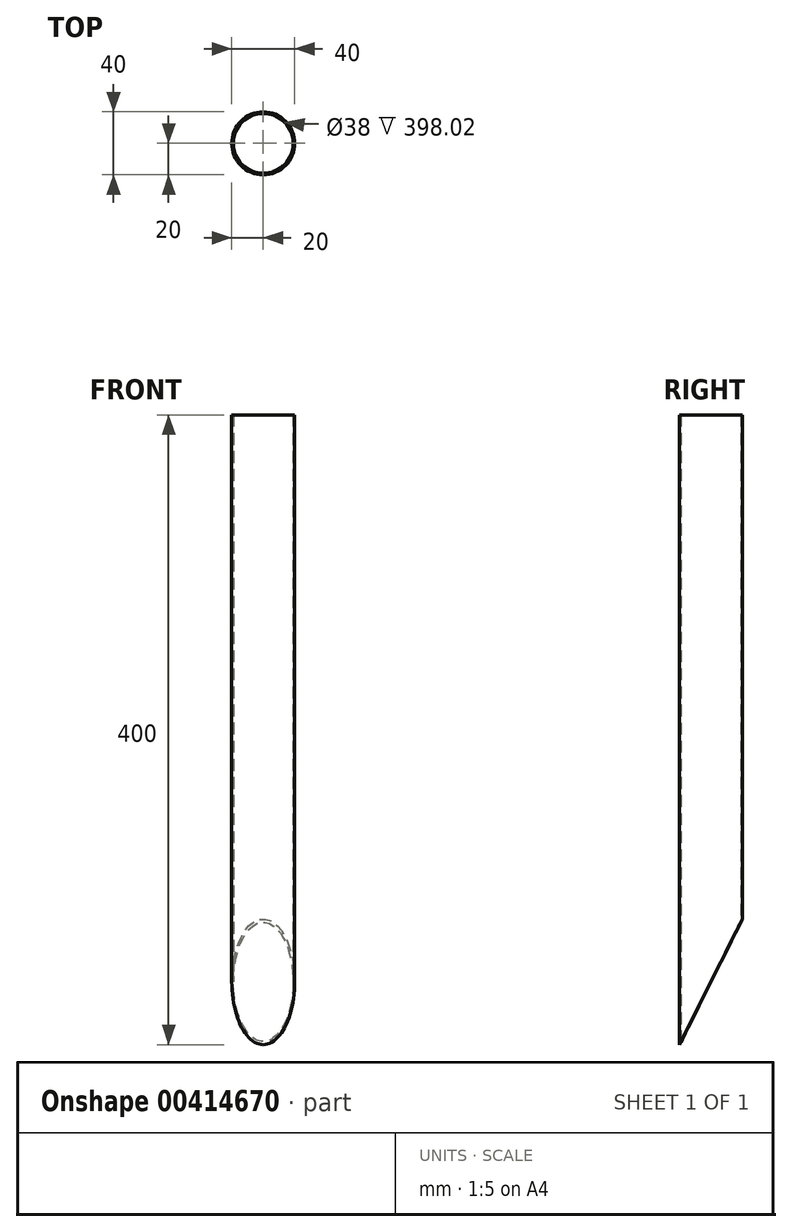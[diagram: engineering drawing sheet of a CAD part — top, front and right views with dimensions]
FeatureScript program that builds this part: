
annotation { "Feature Type Name" : "Feature", "Feature Type Description" : "" }
export const myFeature = defineFeature(function(context is Context, id is Id, definition is map)
    precondition{}
    {
        {
            var Q0;
            Q0=qCreatedBy(makeId("Right.planeOp"),FACE);
            var sketch = newSketch(context, id + "F0", { "sketchPlane" : qUnion([Q0])});
            skLineSegment(sketch, "E0", {"start": v(0, 0) * mm, "end": v(0, -400) * mm});
            skSolve(sketch);
        }
        {
            var Q0;
            Q0=qCreatedBy(makeId("Top.planeOp"),FACE);
            var sketch = newSketch(context, id + "F1", { "sketchPlane" : qUnion([Q0])});
            skCircle(sketch, "E1", {"center": v(0, 0) * mm, "radius": 20 * mm});
            skCircle(sketch, "E2.0", {"center": v(0, 0) * mm, "radius": 19 * mm});
            skSolve(sketch);
        }
        {
            var Q0;
            Q0=makeQuery(id+"F1.imprint","IMPRINT",FACE,{"disambiguationData":[TD([[makeQuery(id+"F1.imprint","IMPRINT",EDGE,{"derivedFrom":sQuery(id+"F1.wireOp",EDGE,"E1")}),1.0]])]});
            var Q1;
            Q1=sQuery(id+"F0.wireOp",EDGE,"E0");
            sweep(context, id + "F2", {"profiles" : qUnion([Q0]), "path" : qUnion([Q1])});
        }
        {
            var Q0;
            Q0=qCreatedBy(makeId("Right.planeOp"),FACE);
            cPlane(context, id + "F3", {"entities" : qUnion([Q0]), "cplaneType" : CPlaneType.OFFSET, "offset" : 20 * mm, "width" : 150 * mm, "height" : 150 * mm});
        }
        {
            var Q0;
            Q0=qCreatedBy(id+"F3.planeOp",FACE);
            var sketch = newSketch(context, id + "F4", { "sketchPlane" : qUnion([Q0])});
            skLineSegment(sketch, "E3", {"start": v(-20, -400) * mm, "end": v(-20, 0) * mm});
            skLineSegment(sketch, "E4", {"start": v(20, 0) * mm, "end": v(20, -400) * mm});
            skLineSegment(sketch, "E5.0", {"start": v(20, -400) * mm, "end": v(-20, -400) * mm});
            skLineSegment(sketch, "E6", {"start": v(-20, -400) * mm, "end": v(20, -320) * mm});
            skSolve(sketch);
        }
        {
            var Q0;
            {var subQ0=sQuery(id+"F4.wireOp",EDGE,"E5.0");Q0=makeQuery(id+"F4.imprint","IMPRINT",FACE,{"disambiguationData":[TD([[makeQuery(id+"F4.imprint","IMPRINT",EDGE,{"derivedFrom":subQ0}),-1.0]])]});}
            extrude(context, id + "F5", {"entities" : qUnion([Q0]), "operationType" : NewBodyOperationType.REMOVE, "endBound" : BoundingType.THROUGH_ALL, "oppositeDirection" : true, "depth" : 25 * mm});
        }
    });
